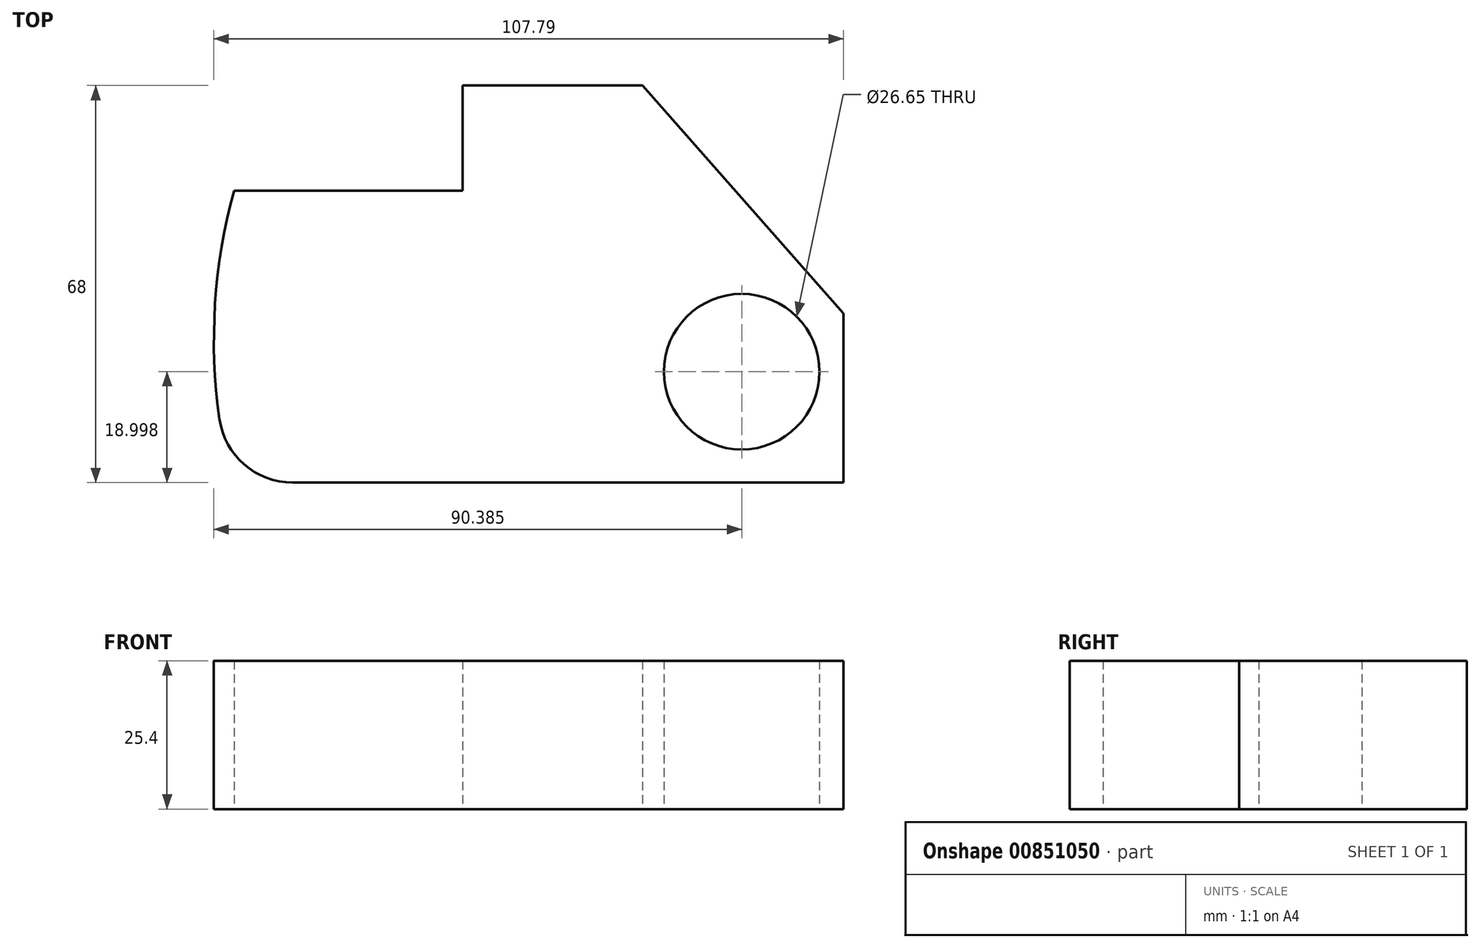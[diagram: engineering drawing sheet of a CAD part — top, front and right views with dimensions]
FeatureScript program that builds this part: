
annotation { "Feature Type Name" : "Feature", "Feature Type Description" : "" }
export const myFeature = defineFeature(function(context is Context, id is Id, definition is map)
    precondition{}
    {
        {
            var Q0;
            Q0=qCreatedBy(makeId("Top.planeOp"),FACE);
            var sketch = newSketch(context, id + "F0", { "sketchPlane" : qUnion([Q0])});
            skLineSegment(sketch, "E0", {"start": v(-49.34, 15.7) * mm, "end": v(-10.2, 15.7) * mm});
            skLineSegment(sketch, "E1", {"start": v(-10.2, 15.7) * mm, "end": v(-10.2, 33.7) * mm});
            skLineSegment(sketch, "E2", {"start": v(-10.2, 33.7) * mm, "end": v(20.6, 33.7) * mm});
            skLineSegment(sketch, "E3", {"start": v(20.6, 33.7) * mm, "end": v(55, -5.3) * mm});
            skLineSegment(sketch, "E4", {"start": v(55, -5.3) * mm, "end": v(55, -34.3) * mm});
            skLineSegment(sketch, "E5", {"start": v(55, -34.3) * mm, "end": v(-49.66, -34.3) * mm});
            skArc(sketch, "E6", {"start": v(-49.34, 15.7) * mm, "mid": v(-52.77, -9.28) * mm, "end": v(-49.66, -34.3) * mm});
            skCircle(sketch, "E7", {"center": v(37.6, -15.3) * mm, "radius": 13.32 * mm});
            skSolve(sketch);
        }
        {
            var Q0;
            Q0=makeQuery(id+"F0.imprint","IMPRINT",FACE,{"disambiguationData":[TD([[makeQuery(id+"F0.imprint","IMPRINT",EDGE,{"derivedFrom":sQuery(id+"F0.wireOp",EDGE,"E0")}),-1.0]])]});
            extrude(context, id + "F1", {"entities" : qUnion([Q0]), "depth" : 25.4 * mm, "offsetDistance" : 25.4 * mm});
        }
        {
            var Q0;
            Q0=makeQuery(id+"F1.opExtrude","SWEPT_EDGE",EDGE,{"disambiguationData":[OSD([sQuery(id+"F0.wireOp",EDGE,"E5"),sQuery(id+"F0.wireOp",EDGE,"E6")])]});
            fillet(context, id + "F2", {"entities" : qUnion([Q0]), "radius" : 12.7 * mm, "tangentPropagation" : true, "allowEdgeOverflow" : false});
        }
    });
